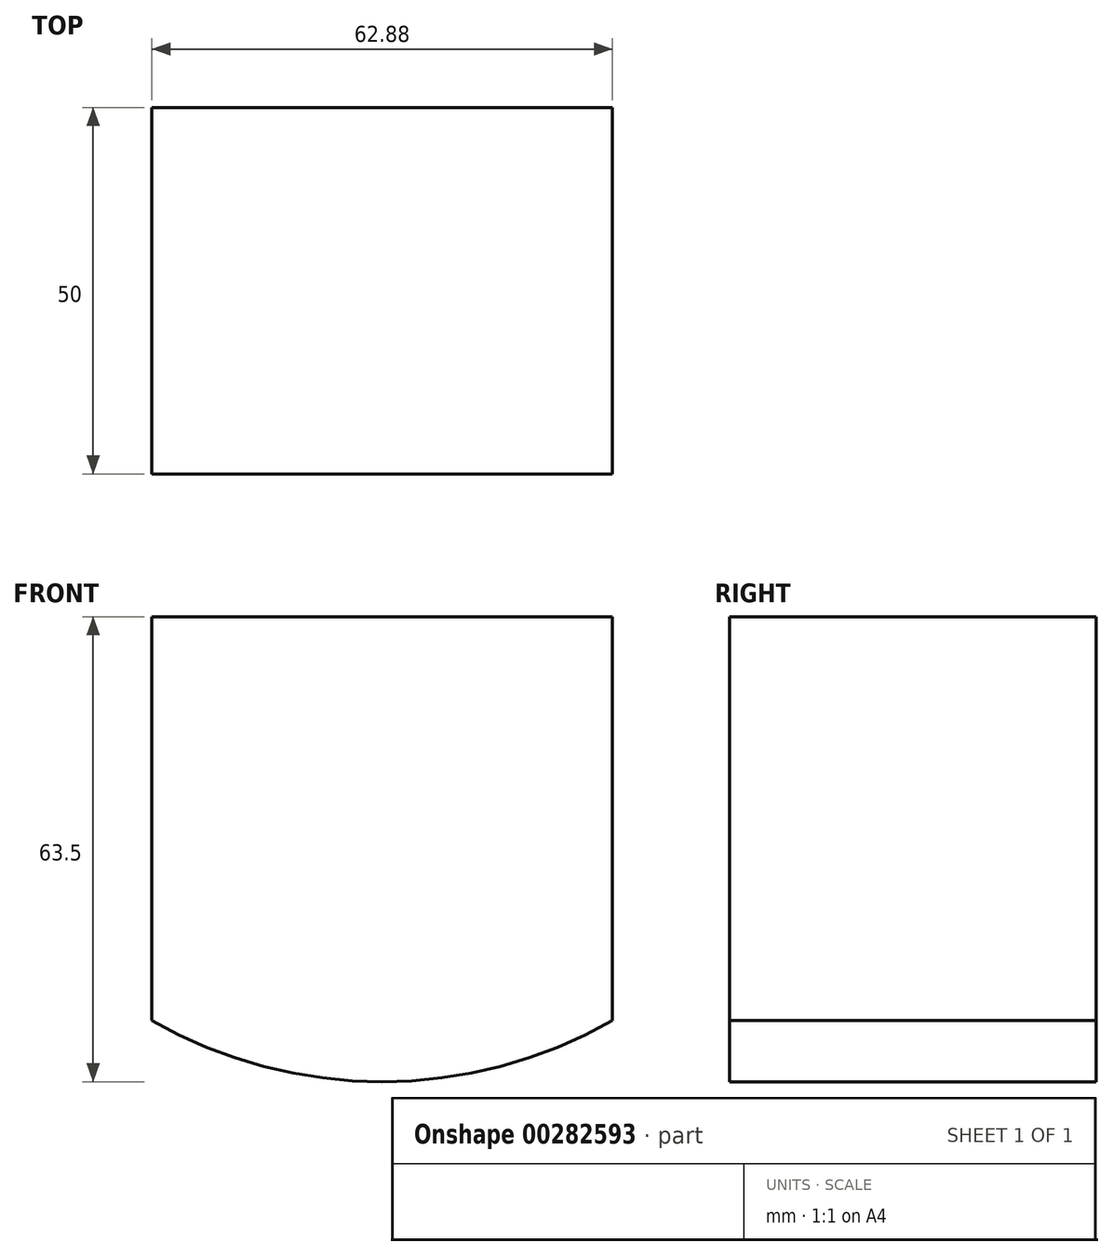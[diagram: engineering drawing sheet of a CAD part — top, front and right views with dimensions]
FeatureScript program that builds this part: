
annotation { "Feature Type Name" : "Feature", "Feature Type Description" : "" }
export const myFeature = defineFeature(function(context is Context, id is Id, definition is map)
    precondition{}
    {
        {
            var Q0;
            Q0=qCreatedBy(makeId("Front.planeOp"),FACE);
            var sketch = newSketch(context, id + "F0", { "sketchPlane" : qUnion([Q0])});
            skCircle(sketch, "E0", {"center": v(0, 0) * mm, "radius": 69.85 * mm, "construction": true});
            skArc(sketch, "E1", {"start": v(-31.44, -55.17) * mm, "mid": v(0, -63.5) * mm, "end": v(31.44, -55.17) * mm});
            skLineSegment(sketch, "E2", {"start": v(-31.44, -55.17) * mm, "end": v(-31.44, 0) * mm});
            skLineSegment(sketch, "E3", {"start": v(-31.44, 0) * mm, "end": v(31.44, 0) * mm});
            skLineSegment(sketch, "E4", {"start": v(31.44, 0) * mm, "end": v(31.44, -55.17) * mm});
            skLineSegment(sketch, "E5", {"start": v(0, -69.85) * mm, "end": v(0, 0) * mm, "construction": true});
            skSolve(sketch);
        }
        {
            var Q0;
            Q0=makeQuery(id+"F0.imprint","IMPRINT",FACE,{"disambiguationData":[TD([[makeQuery(id+"F0.imprint","IMPRINT",EDGE,{"derivedFrom":sQuery(id+"F0.wireOp",EDGE,"E1")}),1.0]])]});
            extrude(context, id + "F1", {"entities" : qUnion([Q0]), "depth" : 50 * mm});
        }
    });
